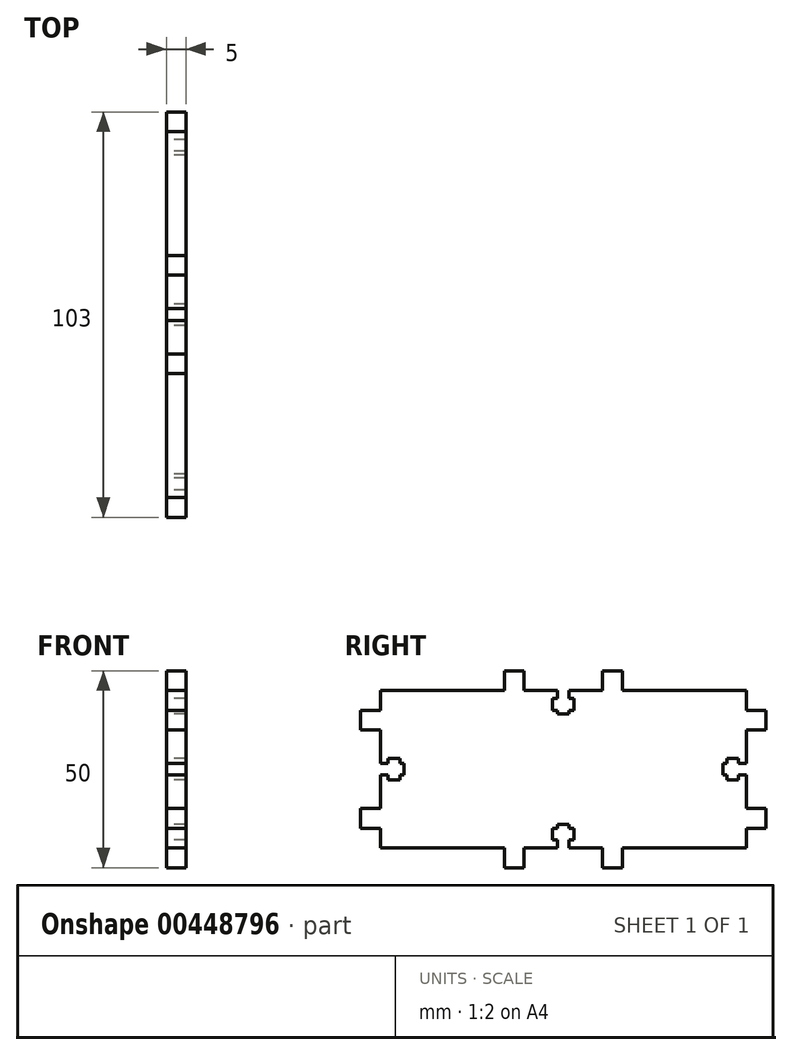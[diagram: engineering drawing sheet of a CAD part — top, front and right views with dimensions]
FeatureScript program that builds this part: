
annotation { "Feature Type Name" : "Feature", "Feature Type Description" : "" }
export const myFeature = defineFeature(function(context is Context, id is Id, definition is map)
    precondition{}
    {
        {
            assignVariable(context, id + "F0", {"name" : "thickness", "anyValue" : 5});
        }
        {
            var Q0;
            Q0=qCreatedBy(makeId("Right.planeOp"),FACE);
            var sketch = newSketch(context, id + "F1", { "sketchPlane" : qUnion([Q0])});
            skLineSegment(sketch, "E0.bottom", {"start": v(0, 0) * mm, "end": v(31.5, 0) * mm});
            skLineSegment(sketch, "E0.top", {"start": v(0, 40) * mm, "end": v(31.5, 40) * mm});
            skLineSegment(sketch, "E0.left", {"start": v(0, 0) * mm, "end": v(0, 5) * mm});
            skLineSegment(sketch, "E0.right", {"start": v(93, 0) * mm, "end": v(93, 5) * mm});
            skLineSegment(sketch, "E1.0", {"start": v(-5, -5) * mm, "end": v(-5, 45) * mm, "construction": true});
            skLineSegment(sketch, "E1.1", {"start": v(-5, -5) * mm, "end": v(98, -5) * mm, "construction": true});
            skLineSegment(sketch, "E1.2", {"start": v(98, -5) * mm, "end": v(98, 45) * mm, "construction": true});
            skLineSegment(sketch, "E1.3", {"start": v(-5, 45) * mm, "end": v(98, 45) * mm, "construction": true});
            skLineSegment(sketch, "E2", {"start": v(0, 35) * mm, "end": v(-5, 35) * mm});
            skLineSegment(sketch, "E3", {"start": v(-5, 35) * mm, "end": v(-5, 30) * mm});
            skLineSegment(sketch, "E4", {"start": v(-5, 30) * mm, "end": v(0, 30) * mm});
            skLineSegment(sketch, "E5", {"start": v(0, 10) * mm, "end": v(-5, 10) * mm});
            skLineSegment(sketch, "E6", {"start": v(-5, 10) * mm, "end": v(-5, 5) * mm});
            skLineSegment(sketch, "E7", {"start": v(-5, 5) * mm, "end": v(0, 5) * mm});
            skLineSegment(sketch, "E8", {"start": v(0, 21.5) * mm, "end": v(2, 21.5) * mm});
            skLineSegment(sketch, "E9", {"start": v(2, 21.5) * mm, "end": v(2, 22.75) * mm});
            skLineSegment(sketch, "E10", {"start": v(2, 22.75) * mm, "end": v(5, 22.75) * mm});
            skLineSegment(sketch, "E11", {"start": v(5, 22.75) * mm, "end": v(5, 21.5) * mm});
            skLineSegment(sketch, "E12", {"start": v(5, 21.5) * mm, "end": v(6, 21.5) * mm});
            skLineSegment(sketch, "E13", {"start": v(6, 21.5) * mm, "end": v(6, 18.5) * mm});
            skLineSegment(sketch, "E14", {"start": v(6, 18.5) * mm, "end": v(5, 18.5) * mm});
            skLineSegment(sketch, "E15", {"start": v(5, 18.5) * mm, "end": v(5, 17.25) * mm});
            skLineSegment(sketch, "E16", {"start": v(5, 17.25) * mm, "end": v(2, 17.25) * mm});
            skLineSegment(sketch, "E17", {"start": v(2, 17.25) * mm, "end": v(2, 18.5) * mm});
            skLineSegment(sketch, "E18", {"start": v(2, 18.5) * mm, "end": v(0, 18.5) * mm});
            skPoint(sketch, "E19", {"position": v(6, 20) * mm});
            skLineSegment(sketch, "E20.trimOffspring", {"start": v(0, 30) * mm, "end": v(0, 21.5) * mm});
            skLineSegment(sketch, "E21.trimOffspring", {"start": v(0, 18.5) * mm, "end": v(0, 10) * mm});
            skPoint(sketch, "E22", {"position": v(0, 20) * mm});
            skLineSegment(sketch, "E23", {"start": v(46.5, 45) * mm, "end": v(46.5, -5) * mm, "construction": true});
            skLineSegment(sketch, "E24", {"start": v(0, 20) * mm, "end": v(93, 20) * mm, "construction": true});
            skLineSegment(sketch, "E25.MirrorCS", {"start": v(91, 18.5) * mm, "end": v(93, 18.5) * mm});
            skLineSegment(sketch, "E26.MirrorCS", {"start": v(88, 18.5) * mm, "end": v(88, 17.25) * mm});
            skLineSegment(sketch, "E27.MirrorCS", {"start": v(88, 22.75) * mm, "end": v(88, 21.5) * mm});
            skLineSegment(sketch, "E28.MirrorCS", {"start": v(93, 21.5) * mm, "end": v(91, 21.5) * mm});
            skLineSegment(sketch, "E29.MirrorCS", {"start": v(91, 21.5) * mm, "end": v(91, 22.75) * mm});
            skLineSegment(sketch, "E30.MirrorCS", {"start": v(91, 17.25) * mm, "end": v(91, 18.5) * mm});
            skLineSegment(sketch, "E31.MirrorCS", {"start": v(88, 21.5) * mm, "end": v(87, 21.5) * mm});
            skLineSegment(sketch, "E32.MirrorCS", {"start": v(87, 18.5) * mm, "end": v(88, 18.5) * mm});
            skLineSegment(sketch, "E33.MirrorCS", {"start": v(87, 21.5) * mm, "end": v(87, 18.5) * mm});
            skLineSegment(sketch, "E34.MirrorCS", {"start": v(91, 22.75) * mm, "end": v(88, 22.75) * mm});
            skLineSegment(sketch, "E35.MirrorCS", {"start": v(93, 18.5) * mm, "end": v(93, 10) * mm});
            skPoint(sketch, "E36.MirrorP", {"position": v(87, 20) * mm});
            skLineSegment(sketch, "E37.MirrorCS", {"start": v(98, 5) * mm, "end": v(93, 5) * mm});
            skLineSegment(sketch, "E38.MirrorCS", {"start": v(93, 10) * mm, "end": v(98, 10) * mm});
            skLineSegment(sketch, "E39.MirrorCS", {"start": v(98, 30) * mm, "end": v(93, 30) * mm});
            skLineSegment(sketch, "E40.MirrorCS", {"start": v(98, 35) * mm, "end": v(98, 30) * mm});
            skLineSegment(sketch, "E41.MirrorCS", {"start": v(98, 10) * mm, "end": v(98, 5) * mm});
            skLineSegment(sketch, "E42.MirrorCS", {"start": v(93, 30) * mm, "end": v(93, 21.5) * mm});
            skLineSegment(sketch, "E43.MirrorCS", {"start": v(93, 35) * mm, "end": v(98, 35) * mm});
            skPoint(sketch, "E44.MirrorP", {"position": v(93, 20) * mm});
            skLineSegment(sketch, "E45.MirrorCS", {"start": v(88, 17.25) * mm, "end": v(91, 17.25) * mm});
            skLineSegment(sketch, "E46.trimOffspring", {"start": v(0, 35) * mm, "end": v(0, 40) * mm});
            skLineSegment(sketch, "E47.trimOffspring", {"start": v(0, 21.5) * mm, "end": v(0, 30) * mm});
            skLineSegment(sketch, "E48.trimOffspring", {"start": v(0, 10) * mm, "end": v(0, 18.5) * mm});
            skLineSegment(sketch, "E49.trimOffspring", {"start": v(93, 21.5) * mm, "end": v(93, 30) * mm});
            skLineSegment(sketch, "E50.trimOffspring", {"start": v(93, 35) * mm, "end": v(93, 40) * mm});
            skLineSegment(sketch, "E51.trimOffspring", {"start": v(93, 10) * mm, "end": v(93, 18.5) * mm});
            skLineSegment(sketch, "E52", {"start": v(61.5, 40) * mm, "end": v(61.5, 45) * mm});
            skLineSegment(sketch, "E53", {"start": v(61.5, 45) * mm, "end": v(56.5, 45) * mm});
            skLineSegment(sketch, "E54", {"start": v(56.5, 45) * mm, "end": v(56.5, 40) * mm});
            skLineSegment(sketch, "E55", {"start": v(36.5, 40) * mm, "end": v(36.5, 45) * mm});
            skLineSegment(sketch, "E56", {"start": v(36.5, 45) * mm, "end": v(31.5, 45) * mm});
            skLineSegment(sketch, "E57", {"start": v(31.5, 45) * mm, "end": v(31.5, 40) * mm});
            skLineSegment(sketch, "E58", {"start": v(48, 40) * mm, "end": v(48, 38) * mm});
            skLineSegment(sketch, "E59", {"start": v(48, 38) * mm, "end": v(49.25, 38) * mm});
            skLineSegment(sketch, "E60", {"start": v(49.25, 38) * mm, "end": v(49.25, 35) * mm});
            skLineSegment(sketch, "E61", {"start": v(49.25, 35) * mm, "end": v(48, 35) * mm});
            skLineSegment(sketch, "E62", {"start": v(48, 35) * mm, "end": v(48, 34) * mm});
            skLineSegment(sketch, "E63", {"start": v(48, 34) * mm, "end": v(45, 34) * mm});
            skLineSegment(sketch, "E64", {"start": v(45, 34) * mm, "end": v(45, 35) * mm});
            skLineSegment(sketch, "E65", {"start": v(45, 35) * mm, "end": v(43.75, 35) * mm});
            skLineSegment(sketch, "E66", {"start": v(43.75, 35) * mm, "end": v(43.75, 38) * mm});
            skLineSegment(sketch, "E67", {"start": v(43.75, 38) * mm, "end": v(45, 38) * mm});
            skLineSegment(sketch, "E68", {"start": v(45, 38) * mm, "end": v(45, 40) * mm});
            skPoint(sketch, "E69", {"position": v(46.5, 34) * mm});
            skLineSegment(sketch, "E70.trimOffspring", {"start": v(56.5, 40) * mm, "end": v(48, 40) * mm});
            skLineSegment(sketch, "E71.trimOffspring", {"start": v(45, 40) * mm, "end": v(36.5, 40) * mm});
            skLineSegment(sketch, "E72.trimOffspring", {"start": v(48, 40) * mm, "end": v(56.5, 40) * mm});
            skLineSegment(sketch, "E73.trimOffspring", {"start": v(36.5, 40) * mm, "end": v(45, 40) * mm});
            skPoint(sketch, "E74", {"position": v(46.5, 40) * mm});
            skLineSegment(sketch, "E75.trimOffspring", {"start": v(61.5, 40) * mm, "end": v(93, 40) * mm});
            skLineSegment(sketch, "E76.MirrorCS", {"start": v(45, 6) * mm, "end": v(45, 5) * mm});
            skLineSegment(sketch, "E77.MirrorCS", {"start": v(48, 5) * mm, "end": v(48, 6) * mm});
            skLineSegment(sketch, "E78.MirrorCS", {"start": v(48, 0) * mm, "end": v(56.5, 0) * mm});
            skLineSegment(sketch, "E79.MirrorCS", {"start": v(45, 5) * mm, "end": v(43.75, 5) * mm});
            skLineSegment(sketch, "E80.MirrorCS", {"start": v(43.75, 2) * mm, "end": v(45, 2) * mm});
            skLineSegment(sketch, "E81.MirrorCS", {"start": v(45, 2) * mm, "end": v(45, 0) * mm});
            skLineSegment(sketch, "E82.MirrorCS", {"start": v(49.25, 5) * mm, "end": v(48, 5) * mm});
            skLineSegment(sketch, "E83.MirrorCS", {"start": v(48, 0) * mm, "end": v(48, 2) * mm});
            skLineSegment(sketch, "E84.MirrorCS", {"start": v(36.5, 0) * mm, "end": v(45, 0) * mm});
            skLineSegment(sketch, "E85.MirrorCS", {"start": v(48, 2) * mm, "end": v(49.25, 2) * mm});
            skLineSegment(sketch, "E86.MirrorCS", {"start": v(48, 6) * mm, "end": v(45, 6) * mm});
            skLineSegment(sketch, "E87.MirrorCS", {"start": v(56.5, 0) * mm, "end": v(48, 0) * mm});
            skLineSegment(sketch, "E88.MirrorCS", {"start": v(49.25, 2) * mm, "end": v(49.25, 5) * mm});
            skLineSegment(sketch, "E89.MirrorCS", {"start": v(36.5, 0) * mm, "end": v(36.5, -5) * mm});
            skPoint(sketch, "E90.MirrorP", {"position": v(46.5, 0) * mm});
            skLineSegment(sketch, "E91.MirrorCS", {"start": v(45, 0) * mm, "end": v(36.5, 0) * mm});
            skLineSegment(sketch, "E92.MirrorCS", {"start": v(56.5, -5) * mm, "end": v(56.5, 0) * mm});
            skPoint(sketch, "E93.MirrorP", {"position": v(46.5, 6) * mm});
            skLineSegment(sketch, "E94.MirrorCS", {"start": v(61.5, -5) * mm, "end": v(56.5, -5) * mm});
            skLineSegment(sketch, "E95.MirrorCS", {"start": v(36.5, -5) * mm, "end": v(31.5, -5) * mm});
            skLineSegment(sketch, "E96.MirrorCS", {"start": v(61.5, 0) * mm, "end": v(61.5, -5) * mm});
            skLineSegment(sketch, "E97.MirrorCS", {"start": v(31.5, -5) * mm, "end": v(31.5, 0) * mm});
            skLineSegment(sketch, "E98.MirrorCS", {"start": v(43.75, 5) * mm, "end": v(43.75, 2) * mm});
            skLineSegment(sketch, "E99.trimOffspring", {"start": v(61.5, 0) * mm, "end": v(93, 0) * mm});
            skSolve(sketch);
        }
        {
            var Q0;
            Q0=makeQuery(id+"F1.imprint","IMPRINT",FACE,{"disambiguationData":[TD([[makeQuery(id+"F1.imprint","IMPRINT",EDGE,{"derivedFrom":sQuery(id+"F1.wireOp",EDGE,"E0.bottom")}),1.0]])]});
            extrude(context, id + "F2", {"entities" : qUnion([Q0]), "depth" : (getVariable(context, 'thickness')) * mm});
        }
    });
